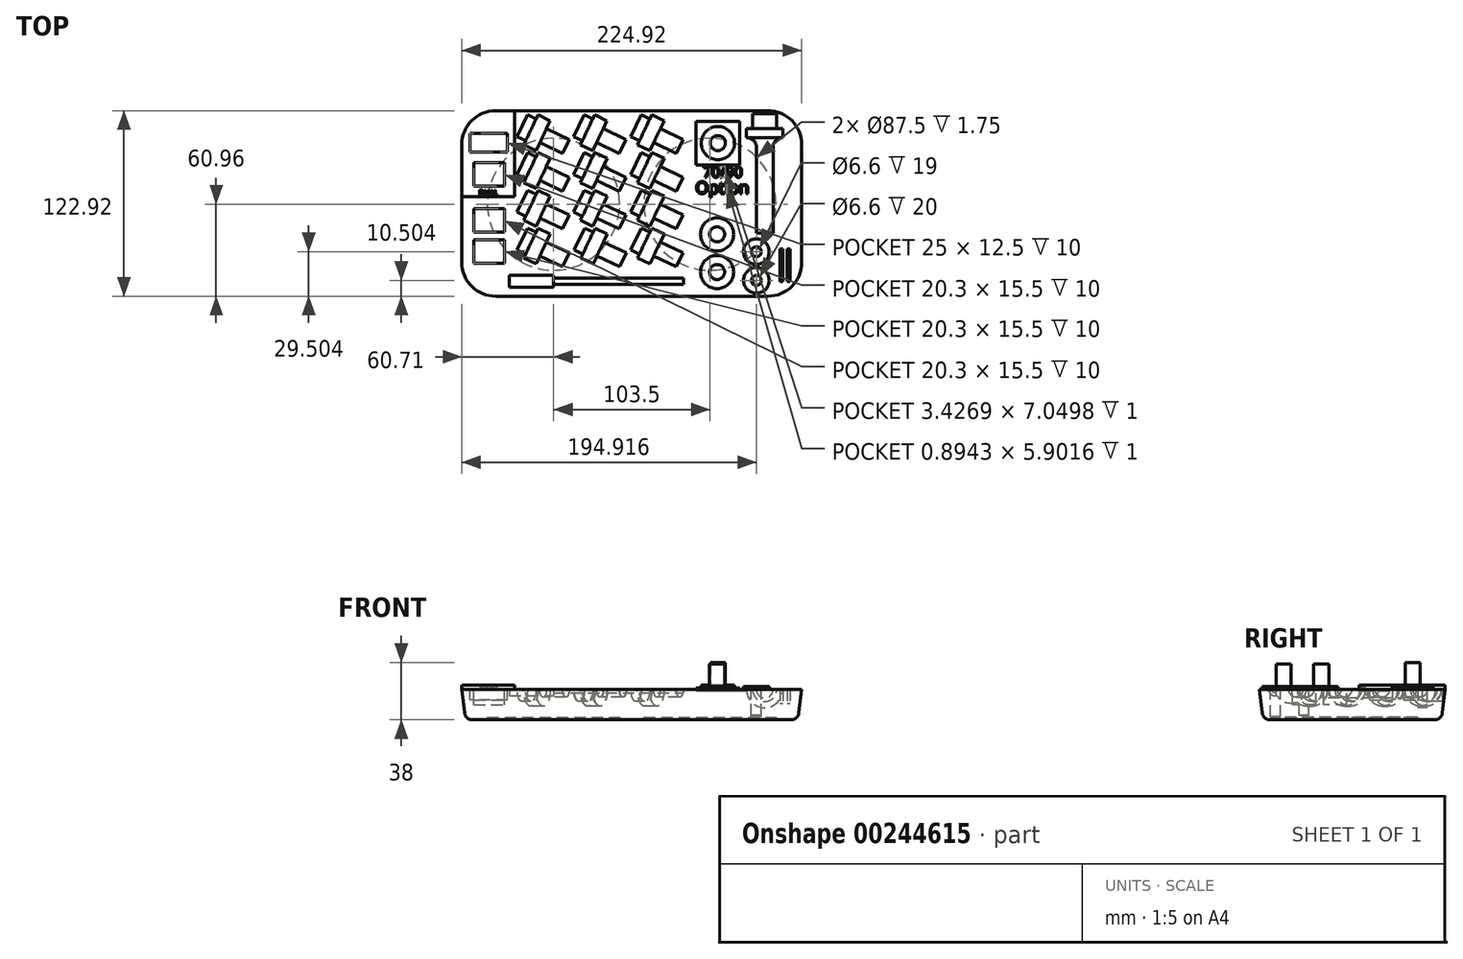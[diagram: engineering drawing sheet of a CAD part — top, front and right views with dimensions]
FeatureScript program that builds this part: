
annotation { "Feature Type Name" : "Feature", "Feature Type Description" : "" }
export const myFeature = defineFeature(function(context is Context, id is Id, definition is map)
    precondition{}
    {
        {
            var Q0;
            Q0=qCreatedBy(makeId("Top.planeOp"),FACE);
            var sketch = newSketch(context, id + "F0", { "sketchPlane" : qUnion([Q0])});
            skLineSegment(sketch, "E0.bottom", {"start": v(20, 0) * mm, "end": v(200, 0) * mm});
            skLineSegment(sketch, "E0.top", {"start": v(20, 118) * mm, "end": v(200, 118) * mm});
            skLineSegment(sketch, "E0.left", {"start": v(0, 20) * mm, "end": v(0, 98) * mm});
            skLineSegment(sketch, "E0.right", {"start": v(220, 20) * mm, "end": v(220, 98) * mm});
            skPoint(sketch, "E1.visualSharp", {"position": v(0, 118) * mm});
            skArc(sketch, "E1.filletArc", {"start": v(20, 118) * mm, "mid": v(5.86, 112.14) * mm, "end": v(0, 98) * mm});
            skPoint(sketch, "E2.visualSharp", {"position": v(220, 118) * mm});
            skArc(sketch, "E2.filletArc", {"start": v(220, 98) * mm, "mid": v(214.14, 112.14) * mm, "end": v(200, 118) * mm});
            skPoint(sketch, "E3.visualSharp", {"position": v(0, 0) * mm});
            skArc(sketch, "E3.filletArc", {"start": v(0, 20) * mm, "mid": v(5.86, 5.86) * mm, "end": v(20, 0) * mm});
            skPoint(sketch, "E4.visualSharp", {"position": v(220, 0) * mm});
            skArc(sketch, "E4.filletArc", {"start": v(200, 0) * mm, "mid": v(214.14, 5.86) * mm, "end": v(220, 20) * mm});
            skSolve(sketch);
        }
        {
            var Q0;
            Q0=makeQuery(id+"F0.imprint","IMPRINT",FACE,{"disambiguationData":[TD([[makeQuery(id+"F0.imprint","IMPRINT",EDGE,{"derivedFrom":sQuery(id+"F0.wireOp",EDGE,"E0.bottom")}),1.0]])]});
            extrude(context, id + "F1", {"entities" : qUnion([Q0]), "depth" : 20 * mm, "hasDraft" : true, "draftAngle" : 7 * degree});
        }
        {
            var Q0;
            Q0=makeQuery(id+"F1.opExtrude","CAP_FACE",FACE,{"disambiguationData":[OSD([sQuery(id+"F0.wireOp",EDGE,"E0.bottom"),sQuery(id+"F0.wireOp",EDGE,"E0.top"),sQuery(id+"F0.wireOp",EDGE,"E0.left"),sQuery(id+"F0.wireOp",EDGE,"E0.right"),sQuery(id+"F0.wireOp",EDGE,"E1.filletArc"),sQuery(id+"F0.wireOp",EDGE,"E2.filletArc"),sQuery(id+"F0.wireOp",EDGE,"E3.filletArc"),sQuery(id+"F0.wireOp",EDGE,"E4.filletArc")])],"isStart":true});
            fillet(context, id + "F2", {"entities" : qUnion([Q0]), "radius" : 5 * mm, "tangentPropagation" : true, "allowEdgeOverflow" : false});
        }
        {
            var Q0;
            Q0=makeQuery(id+"F1.opExtrude","CAP_FACE",FACE,{"disambiguationData":[OSD([sQuery(id+"F0.wireOp",EDGE,"E0.bottom"),sQuery(id+"F0.wireOp",EDGE,"E0.top"),sQuery(id+"F0.wireOp",EDGE,"E0.left"),sQuery(id+"F0.wireOp",EDGE,"E0.right"),sQuery(id+"F0.wireOp",EDGE,"E1.filletArc"),sQuery(id+"F0.wireOp",EDGE,"E2.filletArc"),sQuery(id+"F0.wireOp",EDGE,"E3.filletArc"),sQuery(id+"F0.wireOp",EDGE,"E4.filletArc")])],"isStart":true});
            var sketch = newSketch(context, id + "F3", { "sketchPlane" : qUnion([Q0])});
            skLineSegment(sketch, "E5.bottom", {"start": v(0, 0) * mm, "end": v(58.25, 0) * mm, "construction": true});
            skLineSegment(sketch, "E5.top", {"start": v(0, -58.5) * mm, "end": v(58.25, -58.5) * mm, "construction": true});
            skLineSegment(sketch, "E5.left", {"start": v(0, 0) * mm, "end": v(0, -58.5) * mm, "construction": true});
            skLineSegment(sketch, "E5.right", {"start": v(58.25, 0) * mm, "end": v(58.25, -58.5) * mm, "construction": true});
            skLineSegment(sketch, "E6.bottom", {"start": v(0, 0) * mm, "end": v(161.75, 0) * mm, "construction": true});
            skLineSegment(sketch, "E6.top", {"start": v(0, -58.5) * mm, "end": v(161.75, -58.5) * mm, "construction": true});
            skLineSegment(sketch, "E6.right", {"start": v(161.75, 0) * mm, "end": v(161.75, -58.5) * mm, "construction": true});
            skCircle(sketch, "E7", {"center": v(58.25, -58.5) * mm, "radius": 43.75 * mm});
            skCircle(sketch, "E8", {"center": v(161.75, -58.5) * mm, "radius": 43.75 * mm});
            skSolve(sketch);
        }
        {
            var Q0;
            Q0=qSketchRegion(id+"F3",true);
            extrude(context, id + "F4", {"entities" : qUnion([Q0]), "operationType" : NewBodyOperationType.REMOVE, "oppositeDirection" : true, "depth" : 1.75 * mm});
        }
        {
            var Q0;
            Q0=makeQuery(id+"F1.opExtrude","CAP_FACE",FACE,{"disambiguationData":[OSD([sQuery(id+"F0.wireOp",EDGE,"E0.bottom"),sQuery(id+"F0.wireOp",EDGE,"E0.top"),sQuery(id+"F0.wireOp",EDGE,"E0.left"),sQuery(id+"F0.wireOp",EDGE,"E0.right"),sQuery(id+"F0.wireOp",EDGE,"E1.filletArc"),sQuery(id+"F0.wireOp",EDGE,"E2.filletArc"),sQuery(id+"F0.wireOp",EDGE,"E3.filletArc"),sQuery(id+"F0.wireOp",EDGE,"E4.filletArc")])],"isStart":false});
            var sketch = newSketch(context, id + "F5", { "sketchPlane" : qUnion([Q0])});
            skLineSegment(sketch, "E9.bottom", {"start": v(-2.46, 63.45) * mm, "end": v(32.54, 63.45) * mm});
            skLineSegment(sketch, "E9.top", {"start": v(-2.46, 120.46) * mm, "end": v(32.54, 120.46) * mm});
            skLineSegment(sketch, "E9.left", {"start": v(-2.46, 63.45) * mm, "end": v(-2.46, 120.46) * mm});
            skLineSegment(sketch, "E9.right", {"start": v(32.54, 63.45) * mm, "end": v(32.54, 120.46) * mm});
            skSolve(sketch);
        }
        {
            var Q0;
            {var subQ1=sQuery(id+"F5.wireOp",EDGE,"E9.bottom");Q0=makeQuery(id+"F5.imprint","IMPRINT",FACE,{"disambiguationData":[TD([[makeQuery(id+"F5.imprint","IMPRINT",EDGE,{"derivedFrom":subQ1}),1.0]])]});}
            extrude(context, id + "F6", {"entities" : qUnion([Q0]), "operationType" : NewBodyOperationType.ADD, "depth" : 3 * mm});
        }
        {
            var Q0;
            Q0=makeQuery(id+"F6.opExtrude","CAP_FACE",FACE,{"disambiguationData":[OSD([sQuery(id+"F0.wireOp",EDGE,"E1.filletArc"),sQuery(id+"F5.wireOp",EDGE,"E9.bottom"),sQuery(id+"F5.wireOp",EDGE,"E9.top"),sQuery(id+"F5.wireOp",EDGE,"E9.left"),sQuery(id+"F5.wireOp",EDGE,"E9.right")])],"isStart":false});
            var sketch = newSketch(context, id + "F7", { "sketchPlane" : qUnion([Q0])});
            skText(sketch, "E10", { "text": "DUAL\n", "fontName": "OpenSans-Regular.ttf"});
            const initialGuessF7  = {"E10": [0.00892, 0.06446, 1, 0, 0.00342]};
            skSetInitialGuess(sketch, initialGuessF7);
            skSolve(sketch);
        }
        {
            var Q0;
            Q0=qSketchRegion(id+"F7",true);
            extrude(context, id + "F8", {"entities" : qUnion([Q0]), "operationType" : NewBodyOperationType.REMOVE, "oppositeDirection" : true, "depth" : 1 * mm});
        }
        {
            var Q0;
            {var subQ0=sQuery(id+"F5.wireOp",EDGE,"E9.left");var subQ1=sQuery(id+"F5.wireOp",EDGE,"E9.top");var subQ2=sQuery(id+"F5.wireOp",EDGE,"E9.bottom");var subQ3=sQuery(id+"F5.wireOp",EDGE,"E9.right");var subQ4=sQuery(id+"F0.wireOp",EDGE,"E1.filletArc");Q0=makeQuery(id+"F8.boolean.opBoolean","SPLIT",FACE,{"disambiguationData":[TD([makeQuery(id+"F6.opExtrude","SWEPT_FACE",FACE,{"disambiguationData":[OSD([subQ2])]})])],"derivedFrom":makeQuery(id+"F6.opExtrude","CAP_FACE",FACE,{"disambiguationData":[OSD([subQ4,subQ2,subQ1,subQ0,subQ3])],"isStart":false})});}
            var sketch = newSketch(context, id + "F9", { "sketchPlane" : qUnion([Q0])});
            skSolve(sketch);
        }
        {
            var Q0;
            Q0=makeQuery(id+"F9.imprint","IMPRINT",FACE,{"disambiguationData":[TD([[makeQuery(id+"F9.imprint","IMPRINT",EDGE,{"derivedFrom":makeQuery(id+"F6.opExtrude","CAP_EDGE",EDGE,{"disambiguationData":[OSD([sQuery(id+"F5.wireOp",EDGE,"E9.bottom")])],"isStart":false})}),1.0]])]});
            var sketch = newSketch(context, id + "F10", { "sketchPlane" : qUnion([Q0])});
            skLineSegment(sketch, "E11.bottom", {"start": v(5.54, 70.45) * mm, "end": v(25.84, 70.45) * mm});
            skLineSegment(sketch, "E11.top", {"start": v(5.54, 85.95) * mm, "end": v(25.84, 85.95) * mm});
            skLineSegment(sketch, "E11.left", {"start": v(5.54, 70.45) * mm, "end": v(5.54, 85.95) * mm});
            skLineSegment(sketch, "E11.right", {"start": v(25.84, 70.45) * mm, "end": v(25.84, 85.95) * mm});
            skLineSegment(sketch, "E12.bottom", {"start": v(27.82, 92.95) * mm, "end": v(2.82, 92.95) * mm});
            skLineSegment(sketch, "E12.top", {"start": v(27.82, 105.45) * mm, "end": v(2.82, 105.45) * mm});
            skLineSegment(sketch, "E12.left", {"start": v(27.82, 92.95) * mm, "end": v(27.82, 105.45) * mm});
            skLineSegment(sketch, "E12.right", {"start": v(2.82, 92.95) * mm, "end": v(2.82, 105.45) * mm});
            skSolve(sketch);
        }
        {
            var Q0;
            Q0=qSketchRegion(id+"F10",true);
            extrude(context, id + "F11", {"entities" : qUnion([Q0]), "operationType" : NewBodyOperationType.REMOVE, "oppositeDirection" : true, "depth" : 10 * mm});
        }
        {
            var Q0;
            Q0=makeQuery(id+"F1.opExtrude","CAP_FACE",FACE,{"disambiguationData":[OSD([sQuery(id+"F0.wireOp",EDGE,"E0.bottom"),sQuery(id+"F0.wireOp",EDGE,"E0.top"),sQuery(id+"F0.wireOp",EDGE,"E0.left"),sQuery(id+"F0.wireOp",EDGE,"E0.right"),sQuery(id+"F0.wireOp",EDGE,"E1.filletArc"),sQuery(id+"F0.wireOp",EDGE,"E2.filletArc"),sQuery(id+"F0.wireOp",EDGE,"E3.filletArc"),sQuery(id+"F0.wireOp",EDGE,"E4.filletArc")])],"isStart":false});
            var sketch = newSketch(context, id + "F12", { "sketchPlane" : qUnion([Q0])});
            skLineSegment(sketch, "E13.bottom", {"start": v(5.54, 55.45) * mm, "end": v(25.84, 55.45) * mm});
            skLineSegment(sketch, "E13.top", {"start": v(5.54, 39.95) * mm, "end": v(25.84, 39.95) * mm});
            skLineSegment(sketch, "E13.left", {"start": v(5.54, 55.45) * mm, "end": v(5.54, 39.95) * mm});
            skLineSegment(sketch, "E13.right", {"start": v(25.84, 55.45) * mm, "end": v(25.84, 39.95) * mm});
            skLineSegment(sketch, "E14.bottom", {"start": v(5.54, 34.95) * mm, "end": v(25.84, 34.95) * mm});
            skLineSegment(sketch, "E14.top", {"start": v(5.54, 19.45) * mm, "end": v(25.84, 19.45) * mm});
            skLineSegment(sketch, "E14.left", {"start": v(5.54, 34.95) * mm, "end": v(5.54, 19.45) * mm});
            skLineSegment(sketch, "E14.right", {"start": v(25.84, 34.95) * mm, "end": v(25.84, 19.45) * mm});
            skSolve(sketch);
        }
        {
            var Q0;
            Q0=qSketchRegion(id+"F12",true);
            extrude(context, id + "F13", {"entities" : qUnion([Q0]), "operationType" : NewBodyOperationType.REMOVE, "oppositeDirection" : true, "depth" : 10 * mm});
        }
        {
            var Q0;
            Q0=makeQuery(id+"F1.opExtrude","CAP_FACE",FACE,{"disambiguationData":[OSD([sQuery(id+"F0.wireOp",EDGE,"E0.bottom"),sQuery(id+"F0.wireOp",EDGE,"E0.top"),sQuery(id+"F0.wireOp",EDGE,"E0.left"),sQuery(id+"F0.wireOp",EDGE,"E0.right"),sQuery(id+"F0.wireOp",EDGE,"E1.filletArc"),sQuery(id+"F0.wireOp",EDGE,"E2.filletArc"),sQuery(id+"F0.wireOp",EDGE,"E3.filletArc"),sQuery(id+"F0.wireOp",EDGE,"E4.filletArc")])],"isStart":false});
            var sketch = newSketch(context, id + "F14", { "sketchPlane" : qUnion([Q0])});
            skLineSegment(sketch, "E15", {"start": v(37.54, 110.46) * mm, "end": v(67.13, 96.37) * mm, "construction": true});
            skLineSegment(sketch, "E16", {"start": v(37.54, 110.46) * mm, "end": v(40.98, 117.68) * mm});
            skLineSegment(sketch, "E17", {"start": v(40.98, 117.68) * mm, "end": v(46.67, 114.97) * mm});
            skLineSegment(sketch, "E18", {"start": v(46.67, 114.97) * mm, "end": v(47.96, 117.68) * mm});
            skLineSegment(sketch, "E19", {"start": v(47.96, 117.68) * mm, "end": v(56.09, 113.8) * mm});
            skLineSegment(sketch, "E20", {"start": v(56.09, 113.8) * mm, "end": v(53.55, 108.48) * mm});
            skLineSegment(sketch, "E21", {"start": v(53.55, 108.48) * mm, "end": v(68.63, 101.3) * mm});
            skLineSegment(sketch, "E22", {"start": v(68.63, 101.3) * mm, "end": v(66.44, 96.7) * mm});
            skLineSegment(sketch, "E23", {"start": v(66.44, 96.7) * mm, "end": v(37.54, 110.46) * mm});
            skLineSegment(sketch, "E24.bottom", {"start": v(37.54, 110.46) * mm, "end": v(75.04, 110.46) * mm, "construction": true});
            skLineSegment(sketch, "E24.top", {"start": v(37.54, 85.46) * mm, "end": v(75.04, 85.46) * mm, "construction": true});
            skLineSegment(sketch, "E24.left", {"start": v(37.54, 110.46) * mm, "end": v(37.54, 85.46) * mm, "construction": true});
            skLineSegment(sketch, "E24.right", {"start": v(75.04, 110.46) * mm, "end": v(75.04, 85.46) * mm, "construction": true});
            skLineSegment(sketch, "E25", {"start": v(37.54, 85.46) * mm, "end": v(40.98, 92.68) * mm});
            skLineSegment(sketch, "E26", {"start": v(40.98, 92.68) * mm, "end": v(46.67, 89.97) * mm});
            skLineSegment(sketch, "E27", {"start": v(46.67, 89.97) * mm, "end": v(47.96, 92.68) * mm});
            skLineSegment(sketch, "E28", {"start": v(47.96, 92.68) * mm, "end": v(56.09, 88.8) * mm});
            skLineSegment(sketch, "E29", {"start": v(56.09, 88.8) * mm, "end": v(53.55, 83.48) * mm});
            skLineSegment(sketch, "E30", {"start": v(53.55, 83.48) * mm, "end": v(68.63, 76.3) * mm});
            skLineSegment(sketch, "E31", {"start": v(68.63, 76.3) * mm, "end": v(66.44, 71.7) * mm});
            skLineSegment(sketch, "E32", {"start": v(66.44, 71.7) * mm, "end": v(37.54, 85.46) * mm});
            skLineSegment(sketch, "E33.bottom", {"start": v(37.54, 85.46) * mm, "end": v(75.06, 85.46) * mm, "construction": true});
            skLineSegment(sketch, "E33.top", {"start": v(37.54, 60.46) * mm, "end": v(75.06, 60.46) * mm, "construction": true});
            skLineSegment(sketch, "E33.left", {"start": v(37.54, 85.46) * mm, "end": v(37.54, 60.46) * mm, "construction": true});
            skLineSegment(sketch, "E33.right", {"start": v(75.06, 85.46) * mm, "end": v(75.06, 60.46) * mm, "construction": true});
            skLineSegment(sketch, "E34.bottom", {"start": v(37.54, 60.46) * mm, "end": v(75.04, 60.46) * mm, "construction": true});
            skLineSegment(sketch, "E34.top", {"start": v(37.54, 35.46) * mm, "end": v(75.04, 35.46) * mm, "construction": true});
            skLineSegment(sketch, "E34.left", {"start": v(37.54, 60.46) * mm, "end": v(37.54, 35.46) * mm, "construction": true});
            skLineSegment(sketch, "E34.right", {"start": v(75.04, 60.46) * mm, "end": v(75.04, 35.46) * mm, "construction": true});
            skLineSegment(sketch, "E35.bottom", {"start": v(37.54, 35.46) * mm, "end": v(75.34, 35.46) * mm, "construction": true});
            skLineSegment(sketch, "E35.top", {"start": v(37.54, 10.46) * mm, "end": v(75.34, 10.46) * mm, "construction": true});
            skLineSegment(sketch, "E35.left", {"start": v(37.54, 35.46) * mm, "end": v(37.54, 10.46) * mm, "construction": true});
            skLineSegment(sketch, "E35.right", {"start": v(75.34, 35.46) * mm, "end": v(75.34, 10.46) * mm, "construction": true});
            skLineSegment(sketch, "E36.bottom", {"start": v(75.04, 110.46) * mm, "end": v(112.84, 110.46) * mm, "construction": true});
            skLineSegment(sketch, "E36.top", {"start": v(75.04, 85.46) * mm, "end": v(112.84, 85.46) * mm, "construction": true});
            skLineSegment(sketch, "E36.right", {"start": v(112.84, 110.46) * mm, "end": v(112.84, 85.46) * mm, "construction": true});
            skLineSegment(sketch, "E37.bottom", {"start": v(75.06, 85.46) * mm, "end": v(112.84, 85.46) * mm, "construction": true});
            skLineSegment(sketch, "E37.top", {"start": v(75.06, 60.46) * mm, "end": v(112.84, 60.46) * mm, "construction": true});
            skLineSegment(sketch, "E37.right", {"start": v(112.84, 85.46) * mm, "end": v(112.84, 60.46) * mm, "construction": true});
            skLineSegment(sketch, "E38.top", {"start": v(75.06, 35.46) * mm, "end": v(112.84, 35.46) * mm, "construction": true});
            skLineSegment(sketch, "E38.left", {"start": v(75.06, 60.46) * mm, "end": v(75.06, 35.46) * mm, "construction": true});
            skLineSegment(sketch, "E38.right", {"start": v(112.84, 60.46) * mm, "end": v(112.84, 35.46) * mm, "construction": true});
            skLineSegment(sketch, "E39.bottom", {"start": v(75.34, 35.46) * mm, "end": v(112.84, 35.46) * mm, "construction": true});
            skLineSegment(sketch, "E39.top", {"start": v(75.34, 10.46) * mm, "end": v(112.84, 10.46) * mm, "construction": true});
            skLineSegment(sketch, "E39.right", {"start": v(112.84, 35.46) * mm, "end": v(112.84, 10.46) * mm, "construction": true});
            skLineSegment(sketch, "E40.bottom", {"start": v(112.84, 110.46) * mm, "end": v(150.64, 110.46) * mm, "construction": true});
            skLineSegment(sketch, "E40.top", {"start": v(112.84, 85.46) * mm, "end": v(150.64, 85.46) * mm, "construction": true});
            skLineSegment(sketch, "E40.right", {"start": v(150.64, 110.46) * mm, "end": v(150.64, 85.46) * mm, "construction": true});
            skLineSegment(sketch, "E41.top", {"start": v(112.84, 60.46) * mm, "end": v(150.64, 60.46) * mm, "construction": true});
            skLineSegment(sketch, "E41.right", {"start": v(150.64, 85.46) * mm, "end": v(150.64, 60.46) * mm, "construction": true});
            skLineSegment(sketch, "E42.top", {"start": v(112.84, 35.46) * mm, "end": v(150.64, 35.46) * mm, "construction": true});
            skLineSegment(sketch, "E42.right", {"start": v(150.64, 60.46) * mm, "end": v(150.64, 35.46) * mm, "construction": true});
            skLineSegment(sketch, "E43.top", {"start": v(112.84, 10.46) * mm, "end": v(150.64, 10.46) * mm, "construction": true});
            skLineSegment(sketch, "E43.right", {"start": v(150.64, 35.46) * mm, "end": v(150.64, 10.46) * mm, "construction": true});
            skLineSegment(sketch, "E44", {"start": v(37.54, 60.46) * mm, "end": v(40.98, 67.68) * mm});
            skLineSegment(sketch, "E45", {"start": v(37.54, 35.46) * mm, "end": v(40.98, 42.68) * mm});
            skLineSegment(sketch, "E46", {"start": v(75.04, 110.46) * mm, "end": v(78.48, 117.68) * mm});
            skLineSegment(sketch, "E47", {"start": v(75.06, 85.46) * mm, "end": v(78.5, 92.68) * mm});
            skLineSegment(sketch, "E48", {"start": v(75.06, 60.46) * mm, "end": v(78.5, 67.68) * mm});
            skPoint(sketch, "E49.endSnap0", {"position": v(75.06, 47.96) * mm});
            skLineSegment(sketch, "E50", {"start": v(75.34, 35.46) * mm, "end": v(78.78, 42.68) * mm});
            skLineSegment(sketch, "E51", {"start": v(112.84, 35.46) * mm, "end": v(116.28, 42.68) * mm});
            skLineSegment(sketch, "E52", {"start": v(112.84, 60.46) * mm, "end": v(116.28, 67.68) * mm});
            skLineSegment(sketch, "E53", {"start": v(112.84, 85.46) * mm, "end": v(116.28, 92.68) * mm});
            skLineSegment(sketch, "E54", {"start": v(112.84, 110.46) * mm, "end": v(116.28, 117.68) * mm});
            skLineSegment(sketch, "E55", {"start": v(40.98, 67.68) * mm, "end": v(46.67, 64.97) * mm});
            skLineSegment(sketch, "E56", {"start": v(46.67, 64.97) * mm, "end": v(47.96, 67.68) * mm});
            skLineSegment(sketch, "E57", {"start": v(47.96, 67.68) * mm, "end": v(56.09, 63.8) * mm});
            skLineSegment(sketch, "E58", {"start": v(56.09, 63.8) * mm, "end": v(53.55, 58.48) * mm});
            skLineSegment(sketch, "E59", {"start": v(40.98, 42.68) * mm, "end": v(46.67, 39.97) * mm});
            skLineSegment(sketch, "E60", {"start": v(46.67, 39.97) * mm, "end": v(47.96, 42.68) * mm});
            skLineSegment(sketch, "E61", {"start": v(47.96, 42.68) * mm, "end": v(56.09, 38.8) * mm});
            skLineSegment(sketch, "E62", {"start": v(56.09, 38.8) * mm, "end": v(53.55, 33.48) * mm});
            skLineSegment(sketch, "E63", {"start": v(53.55, 33.48) * mm, "end": v(68.63, 26.3) * mm});
            skLineSegment(sketch, "E64", {"start": v(68.63, 26.3) * mm, "end": v(66.44, 21.7) * mm});
            skLineSegment(sketch, "E65", {"start": v(66.44, 21.7) * mm, "end": v(37.54, 35.46) * mm});
            skLineSegment(sketch, "E66", {"start": v(53.55, 58.48) * mm, "end": v(68.63, 51.3) * mm});
            skLineSegment(sketch, "E67", {"start": v(68.63, 51.3) * mm, "end": v(66.44, 46.7) * mm});
            skLineSegment(sketch, "E68", {"start": v(66.44, 46.7) * mm, "end": v(37.54, 60.46) * mm});
            skLineSegment(sketch, "E69", {"start": v(78.48, 117.68) * mm, "end": v(84.17, 114.97) * mm});
            skLineSegment(sketch, "E70", {"start": v(84.17, 114.97) * mm, "end": v(85.46, 117.68) * mm});
            skLineSegment(sketch, "E71", {"start": v(85.46, 117.68) * mm, "end": v(93.59, 113.8) * mm});
            skLineSegment(sketch, "E72", {"start": v(93.59, 113.8) * mm, "end": v(91.05, 108.48) * mm});
            skLineSegment(sketch, "E73", {"start": v(91.05, 108.48) * mm, "end": v(106.13, 101.3) * mm});
            skLineSegment(sketch, "E74", {"start": v(106.13, 101.3) * mm, "end": v(103.94, 96.7) * mm});
            skLineSegment(sketch, "E75", {"start": v(103.94, 96.7) * mm, "end": v(75.04, 110.46) * mm});
            skLineSegment(sketch, "E76", {"start": v(78.5, 92.68) * mm, "end": v(84.19, 89.97) * mm});
            skLineSegment(sketch, "E77", {"start": v(84.19, 89.97) * mm, "end": v(85.48, 92.68) * mm});
            skLineSegment(sketch, "E78", {"start": v(85.48, 92.68) * mm, "end": v(93.6, 88.8) * mm});
            skLineSegment(sketch, "E79", {"start": v(93.6, 88.8) * mm, "end": v(91.07, 83.48) * mm});
            skLineSegment(sketch, "E80", {"start": v(91.07, 83.48) * mm, "end": v(106.14, 76.3) * mm});
            skLineSegment(sketch, "E81", {"start": v(106.14, 76.3) * mm, "end": v(103.95, 71.7) * mm});
            skLineSegment(sketch, "E82", {"start": v(103.95, 71.7) * mm, "end": v(75.06, 85.46) * mm});
            skLineSegment(sketch, "E83", {"start": v(78.5, 67.68) * mm, "end": v(84.19, 64.97) * mm});
            skLineSegment(sketch, "E84", {"start": v(84.19, 64.97) * mm, "end": v(85.48, 67.68) * mm});
            skLineSegment(sketch, "E85", {"start": v(85.48, 67.68) * mm, "end": v(93.6, 63.8) * mm});
            skLineSegment(sketch, "E86", {"start": v(93.6, 63.8) * mm, "end": v(91.07, 58.48) * mm});
            skLineSegment(sketch, "E87", {"start": v(91.07, 58.48) * mm, "end": v(106.14, 51.3) * mm});
            skLineSegment(sketch, "E88", {"start": v(106.14, 51.3) * mm, "end": v(103.95, 46.7) * mm});
            skLineSegment(sketch, "E89", {"start": v(103.95, 46.7) * mm, "end": v(75.06, 60.46) * mm});
            skLineSegment(sketch, "E90", {"start": v(78.78, 42.68) * mm, "end": v(84.47, 39.97) * mm});
            skLineSegment(sketch, "E91", {"start": v(84.47, 39.97) * mm, "end": v(85.76, 42.68) * mm});
            skLineSegment(sketch, "E92", {"start": v(85.76, 42.68) * mm, "end": v(93.88, 38.8) * mm});
            skLineSegment(sketch, "E93", {"start": v(93.88, 38.8) * mm, "end": v(91.35, 33.48) * mm});
            skLineSegment(sketch, "E94", {"start": v(91.35, 33.48) * mm, "end": v(106.42, 26.3) * mm});
            skLineSegment(sketch, "E95", {"start": v(106.42, 26.3) * mm, "end": v(104.23, 21.7) * mm});
            skLineSegment(sketch, "E96", {"start": v(104.23, 21.7) * mm, "end": v(75.34, 35.46) * mm});
            skLineSegment(sketch, "E97", {"start": v(116.28, 117.68) * mm, "end": v(121.97, 114.97) * mm});
            skLineSegment(sketch, "E98", {"start": v(121.97, 114.97) * mm, "end": v(123.26, 117.68) * mm});
            skLineSegment(sketch, "E99", {"start": v(123.26, 117.68) * mm, "end": v(131.38, 113.8) * mm});
            skLineSegment(sketch, "E100", {"start": v(131.38, 113.8) * mm, "end": v(128.85, 108.48) * mm});
            skLineSegment(sketch, "E101", {"start": v(128.85, 108.48) * mm, "end": v(143.92, 101.3) * mm});
            skLineSegment(sketch, "E102", {"start": v(143.92, 101.3) * mm, "end": v(141.73, 96.7) * mm});
            skLineSegment(sketch, "E103", {"start": v(141.73, 96.7) * mm, "end": v(112.84, 110.46) * mm});
            skLineSegment(sketch, "E104", {"start": v(116.28, 92.68) * mm, "end": v(121.97, 89.97) * mm});
            skLineSegment(sketch, "E105", {"start": v(121.97, 89.97) * mm, "end": v(123.26, 92.68) * mm});
            skLineSegment(sketch, "E106", {"start": v(123.26, 92.68) * mm, "end": v(131.38, 88.8) * mm});
            skLineSegment(sketch, "E107", {"start": v(131.38, 88.8) * mm, "end": v(128.85, 83.48) * mm});
            skLineSegment(sketch, "E108", {"start": v(128.85, 83.48) * mm, "end": v(143.92, 76.3) * mm});
            skLineSegment(sketch, "E109", {"start": v(143.92, 76.3) * mm, "end": v(141.73, 71.7) * mm});
            skLineSegment(sketch, "E110", {"start": v(141.73, 71.7) * mm, "end": v(112.84, 85.46) * mm});
            skLineSegment(sketch, "E111", {"start": v(116.28, 67.68) * mm, "end": v(121.97, 64.97) * mm});
            skLineSegment(sketch, "E112", {"start": v(121.97, 64.97) * mm, "end": v(123.26, 67.68) * mm});
            skLineSegment(sketch, "E113", {"start": v(123.26, 67.68) * mm, "end": v(131.38, 63.8) * mm});
            skLineSegment(sketch, "E114", {"start": v(131.38, 63.8) * mm, "end": v(128.85, 58.48) * mm});
            skLineSegment(sketch, "E115", {"start": v(128.85, 58.48) * mm, "end": v(143.92, 51.3) * mm});
            skLineSegment(sketch, "E116", {"start": v(143.92, 51.3) * mm, "end": v(141.73, 46.7) * mm});
            skLineSegment(sketch, "E117", {"start": v(141.73, 46.7) * mm, "end": v(112.84, 60.46) * mm});
            skLineSegment(sketch, "E118", {"start": v(116.28, 42.68) * mm, "end": v(121.97, 39.97) * mm});
            skLineSegment(sketch, "E119", {"start": v(121.97, 39.97) * mm, "end": v(123.26, 42.68) * mm});
            skLineSegment(sketch, "E120", {"start": v(123.26, 42.68) * mm, "end": v(131.38, 38.8) * mm});
            skLineSegment(sketch, "E121", {"start": v(131.38, 38.8) * mm, "end": v(128.85, 33.48) * mm});
            skLineSegment(sketch, "E122", {"start": v(128.85, 33.48) * mm, "end": v(143.92, 26.3) * mm});
            skLineSegment(sketch, "E123", {"start": v(143.92, 26.3) * mm, "end": v(141.73, 21.7) * mm});
            skLineSegment(sketch, "E124", {"start": v(141.73, 21.7) * mm, "end": v(112.84, 35.46) * mm});
            skSolve(sketch);
        }
        {
            var Q0;
            Q0=makeQuery(id+"F14.imprint","IMPRINT",FACE,{"disambiguationData":[TD([[makeQuery(id+"F14.imprint","IMPRINT",EDGE,{"derivedFrom":sQuery(id+"F14.wireOp",EDGE,"E16")}),-1.0]])]});
            var Q1;
            Q1=sQuery(id+"F14.wireOp",EDGE,"E23");
            revolve(context, id + "F15", {"operationType" : NewBodyOperationType.REMOVE, "entities" : qUnion([Q0]), "axis" : qUnion([Q1]), "revolveType" : RevolveType.FULL, "oppositeDirection" : true});
        }
        {
            var Q0;
            Q0=makeQuery(id+"F14.imprint","IMPRINT",FACE,{"disambiguationData":[TD([[makeQuery(id+"F14.imprint","IMPRINT",EDGE,{"derivedFrom":sQuery(id+"F14.wireOp",EDGE,"E25")}),-1.0]])]});
            var Q1;
            Q1=sQuery(id+"F14.wireOp",EDGE,"E32");
            revolve(context, id + "F16", {"operationType" : NewBodyOperationType.REMOVE, "entities" : qUnion([Q0]), "axis" : qUnion([Q1]), "revolveType" : RevolveType.FULL, "oppositeDirection" : true});
        }
        {
            var Q0;
            Q0=makeQuery(id+"F14.imprint","IMPRINT",FACE,{"disambiguationData":[TD([[makeQuery(id+"F14.imprint","IMPRINT",EDGE,{"derivedFrom":sQuery(id+"F14.wireOp",EDGE,"E44")}),-1.0]])]});
            var Q1;
            Q1=sQuery(id+"F14.wireOp",EDGE,"E68");
            revolve(context, id + "F17", {"operationType" : NewBodyOperationType.REMOVE, "entities" : qUnion([Q0]), "axis" : qUnion([Q1]), "revolveType" : RevolveType.FULL, "oppositeDirection" : true});
        }
        {
            var Q0;
            Q0=makeQuery(id+"F14.imprint","IMPRINT",FACE,{"disambiguationData":[TD([[makeQuery(id+"F14.imprint","IMPRINT",EDGE,{"derivedFrom":sQuery(id+"F14.wireOp",EDGE,"E45")}),-1.0]])]});
            var Q1;
            Q1=sQuery(id+"F14.wireOp",EDGE,"E65");
            revolve(context, id + "F18", {"operationType" : NewBodyOperationType.REMOVE, "entities" : qUnion([Q0]), "axis" : qUnion([Q1]), "revolveType" : RevolveType.FULL, "oppositeDirection" : true});
        }
        {
            var Q0;
            Q0=makeQuery(id+"F14.imprint","IMPRINT",FACE,{"disambiguationData":[TD([[makeQuery(id+"F14.imprint","IMPRINT",EDGE,{"derivedFrom":sQuery(id+"F14.wireOp",EDGE,"E46")}),-1.0]])]});
            var Q1;
            Q1=sQuery(id+"F14.wireOp",EDGE,"E75");
            revolve(context, id + "F19", {"operationType" : NewBodyOperationType.REMOVE, "entities" : qUnion([Q0]), "axis" : qUnion([Q1]), "revolveType" : RevolveType.FULL, "oppositeDirection" : true});
        }
        {
            var Q0;
            Q0=makeQuery(id+"F14.imprint","IMPRINT",FACE,{"disambiguationData":[TD([[makeQuery(id+"F14.imprint","IMPRINT",EDGE,{"derivedFrom":sQuery(id+"F14.wireOp",EDGE,"E47")}),-1.0]])]});
            var Q1;
            Q1=sQuery(id+"F14.wireOp",EDGE,"E82");
            revolve(context, id + "F20", {"operationType" : NewBodyOperationType.REMOVE, "entities" : qUnion([Q0]), "axis" : qUnion([Q1]), "revolveType" : RevolveType.FULL, "oppositeDirection" : true});
        }
        {
            var Q0;
            Q0=makeQuery(id+"F14.imprint","IMPRINT",FACE,{"disambiguationData":[TD([[makeQuery(id+"F14.imprint","IMPRINT",EDGE,{"derivedFrom":sQuery(id+"F14.wireOp",EDGE,"E54")}),-1.0]])]});
            var Q1;
            Q1=sQuery(id+"F14.wireOp",EDGE,"E103");
            revolve(context, id + "F21", {"operationType" : NewBodyOperationType.REMOVE, "entities" : qUnion([Q0]), "axis" : qUnion([Q1]), "revolveType" : RevolveType.FULL, "oppositeDirection" : true});
        }
        {
            var Q0;
            Q0=makeQuery(id+"F14.imprint","IMPRINT",FACE,{"disambiguationData":[TD([[makeQuery(id+"F14.imprint","IMPRINT",EDGE,{"derivedFrom":sQuery(id+"F14.wireOp",EDGE,"E51")}),-1.0]])]});
            var Q1;
            Q1=sQuery(id+"F14.wireOp",EDGE,"E124");
            revolve(context, id + "F22", {"operationType" : NewBodyOperationType.REMOVE, "entities" : qUnion([Q0]), "axis" : qUnion([Q1]), "revolveType" : RevolveType.FULL, "oppositeDirection" : true});
        }
        {
            var Q0;
            Q0=makeQuery(id+"F14.imprint","IMPRINT",FACE,{"disambiguationData":[TD([[makeQuery(id+"F14.imprint","IMPRINT",EDGE,{"derivedFrom":sQuery(id+"F14.wireOp",EDGE,"E53")}),-1.0]])]});
            var Q1;
            Q1=sQuery(id+"F14.wireOp",EDGE,"E110");
            revolve(context, id + "F23", {"operationType" : NewBodyOperationType.REMOVE, "entities" : qUnion([Q0]), "axis" : qUnion([Q1]), "revolveType" : RevolveType.FULL, "oppositeDirection" : true});
        }
        {
            var Q0;
            Q0=makeQuery(id+"F14.imprint","IMPRINT",FACE,{"disambiguationData":[TD([[makeQuery(id+"F14.imprint","IMPRINT",EDGE,{"derivedFrom":sQuery(id+"F14.wireOp",EDGE,"E52")}),-1.0]])]});
            var Q1;
            Q1=sQuery(id+"F14.wireOp",EDGE,"E117");
            revolve(context, id + "F24", {"operationType" : NewBodyOperationType.REMOVE, "entities" : qUnion([Q0]), "axis" : qUnion([Q1]), "revolveType" : RevolveType.FULL, "oppositeDirection" : true});
        }
        {
            var Q0;
            Q0=makeQuery(id+"F14.imprint","IMPRINT",FACE,{"disambiguationData":[TD([[makeQuery(id+"F14.imprint","IMPRINT",EDGE,{"derivedFrom":sQuery(id+"F14.wireOp",EDGE,"E48")}),-1.0]])]});
            var Q1;
            Q1=sQuery(id+"F14.wireOp",EDGE,"E89");
            revolve(context, id + "F25", {"operationType" : NewBodyOperationType.REMOVE, "entities" : qUnion([Q0]), "axis" : qUnion([Q1]), "revolveType" : RevolveType.FULL, "oppositeDirection" : true});
        }
        {
            var Q0;
            Q0=makeQuery(id+"F14.imprint","IMPRINT",FACE,{"disambiguationData":[TD([[makeQuery(id+"F14.imprint","IMPRINT",EDGE,{"derivedFrom":sQuery(id+"F14.wireOp",EDGE,"E50")}),-1.0]])]});
            var Q1;
            Q1=sQuery(id+"F14.wireOp",EDGE,"E96");
            revolve(context, id + "F26", {"operationType" : NewBodyOperationType.REMOVE, "entities" : qUnion([Q0]), "axis" : qUnion([Q1]), "revolveType" : RevolveType.FULL, "oppositeDirection" : true});
        }
        {
            var Q0;
            Q0=makeQuery(id+"F14.imprint","IMPRINT",FACE,{"disambiguationData":[TD([[makeQuery(id+"F14.imprint","IMPRINT",EDGE,{"derivedFrom":sQuery(id+"F14.wireOp",EDGE,"E16")}),1.0]])]});
            var sketch = newSketch(context, id + "F27", { "sketchPlane" : qUnion([Q0])});
            skLineSegment(sketch, "E125.bottom", {"start": v(152.46, 113.46) * mm, "end": v(181.46, 113.46) * mm});
            skLineSegment(sketch, "E125.top", {"start": v(152.46, 84.46) * mm, "end": v(181.46, 84.46) * mm});
            skLineSegment(sketch, "E125.left", {"start": v(152.46, 113.46) * mm, "end": v(152.46, 84.46) * mm});
            skLineSegment(sketch, "E125.right", {"start": v(181.46, 113.46) * mm, "end": v(181.46, 84.46) * mm});
            skLineSegment(sketch, "E126", {"start": v(152.46, 84.46) * mm, "end": v(181.46, 113.46) * mm, "construction": true});
            skLineSegment(sketch, "E127", {"start": v(152.46, 113.46) * mm, "end": v(181.46, 84.46) * mm, "construction": true});
            skSolve(sketch);
        }
        {
            var Q0;
            Q0=qSketchRegion(id+"F27",true);
            extrude(context, id + "F28", {"entities" : qUnion([Q0]), "operationType" : NewBodyOperationType.ADD, "depth" : 1 * mm});
        }
        {
            var Q0;
            Q0=makeQuery(id+"F28.opExtrude","CAP_FACE",FACE,{"disambiguationData":[OSD([sQuery(id+"F27.wireOp",EDGE,"E125.bottom"),sQuery(id+"F27.wireOp",EDGE,"E125.top"),sQuery(id+"F27.wireOp",EDGE,"E125.left"),sQuery(id+"F27.wireOp",EDGE,"E125.right")])],"isStart":false});
            var sketch = newSketch(context, id + "F29", { "sketchPlane" : qUnion([Q0])});
            skLineSegment(sketch, "E128", {"start": v(152.46, 84.46) * mm, "end": v(181.46, 113.46) * mm, "construction": true});
            skLineSegment(sketch, "E129", {"start": v(181.46, 113.46) * mm, "end": v(152.46, 113.46) * mm, "construction": true});
            skLineSegment(sketch, "E130", {"start": v(152.46, 113.46) * mm, "end": v(181.46, 84.46) * mm, "construction": true});
            skCircle(sketch, "E131", {"center": v(166.96, 98.96) * mm, "radius": 11 * mm});
            skSolve(sketch);
        }
        {
            var Q0;
            Q0=qSketchRegion(id+"F29",true);
            extrude(context, id + "F30", {"entities" : qUnion([Q0]), "operationType" : NewBodyOperationType.ADD, "depth" : 2 * mm});
        }
        {
            var Q0;
            Q0=makeQuery(id+"F30.opExtrude","CAP_FACE",FACE,{"disambiguationData":[OSD([sQuery(id+"F29.wireOp",EDGE,"E131")])],"isStart":false});
            var sketch = newSketch(context, id + "F31", { "sketchPlane" : qUnion([Q0])});
            skCircle(sketch, "E132", {"center": v(166.96, 98.96) * mm, "radius": 5 * mm});
            skSolve(sketch);
        }
        {
            var Q0;
            Q0=qSketchRegion(id+"F31",true);
            extrude(context, id + "F32", {"entities" : qUnion([Q0]), "operationType" : NewBodyOperationType.ADD, "depth" : 15 * mm});
        }
        {
            var Q0;
            Q0=makeQuery(id+"F14.imprint","IMPRINT",FACE,{"disambiguationData":[TD([[makeQuery(id+"F14.imprint","IMPRINT",EDGE,{"derivedFrom":sQuery(id+"F14.wireOp",EDGE,"E16")}),1.0]])]});
            var sketch = newSketch(context, id + "F33", { "sketchPlane" : qUnion([Q0])});
            skCircle(sketch, "E133", {"center": v(166.46, 38.54) * mm, "radius": 11 * mm});
            skCircle(sketch, "E134", {"center": v(166.46, 13.54) * mm, "radius": 11 * mm});
            skSolve(sketch);
        }
        {
            var Q0;
            Q0=qSketchRegion(id+"F33",true);
            extrude(context, id + "F34", {"entities" : qUnion([Q0]), "operationType" : NewBodyOperationType.ADD, "depth" : 2 * mm});
        }
        {
            var Q0;
            Q0=makeQuery(id+"F34.opExtrude","CAP_FACE",FACE,{"disambiguationData":[OSD([sQuery(id+"F33.wireOp",EDGE,"E133")])],"isStart":false});
            var sketch = newSketch(context, id + "F35", { "sketchPlane" : qUnion([Q0])});
            skCircle(sketch, "E135", {"center": v(166.46, 38.54) * mm, "radius": 5 * mm});
            skSolve(sketch);
        }
        {
            var Q0;
            Q0=makeQuery(id+"F34.opExtrude","CAP_FACE",FACE,{"disambiguationData":[OSD([sQuery(id+"F33.wireOp",EDGE,"E134")])],"isStart":false});
            var sketch = newSketch(context, id + "F36", { "sketchPlane" : qUnion([Q0])});
            skCircle(sketch, "E136", {"center": v(166.46, 13.54) * mm, "radius": 5 * mm});
            skSolve(sketch);
        }
        {
            var Q0;
            Q0=qSketchRegion(id+"F36",true);
            extrude(context, id + "F37", {"entities" : qUnion([Q0]), "operationType" : NewBodyOperationType.ADD, "depth" : 15 * mm});
        }
        {
            var Q0;
            Q0=qSketchRegion(id+"F35",true);
            extrude(context, id + "F38", {"entities" : qUnion([Q0]), "operationType" : NewBodyOperationType.ADD, "depth" : 15 * mm});
        }
        {
            var Q0;
            Q0=makeQuery(id+"F14.imprint","IMPRINT",FACE,{"disambiguationData":[TD([[makeQuery(id+"F14.imprint","IMPRINT",EDGE,{"derivedFrom":sQuery(id+"F14.wireOp",EDGE,"E16")}),1.0]])]});
            var sketch = newSketch(context, id + "F39", { "sketchPlane" : qUnion([Q0])});
            skText(sketch, "E137", { "text": "70/90", "fontName": "OpenSans-Regular.ttf"});
            const initialGuessF39  = {"E137": [0.1571, 0.07634, 1, 0, 0.00711]};
            skSetInitialGuess(sketch, initialGuessF39);
            skSolve(sketch);
        }
        {
            var Q0;
            Q0=qSketchRegion(id+"F39",true);
            extrude(context, id + "F40", {"entities" : qUnion([Q0]), "operationType" : NewBodyOperationType.REMOVE, "oppositeDirection" : true, "depth" : 1 * mm});
        }
        {
            var Q0;
            Q0=makeQuery(id+"F14.imprint","IMPRINT",FACE,{"disambiguationData":[TD([[makeQuery(id+"F14.imprint","IMPRINT",EDGE,{"derivedFrom":sQuery(id+"F14.wireOp",EDGE,"E16")}),1.0]])]});
            var sketch = newSketch(context, id + "F41", { "sketchPlane" : qUnion([Q0])});
            skText(sketch, "E138", { "text": "Option", "fontName": "OpenSans-Regular.ttf"});
            const initialGuessF41  = {"E138": [0.15217, 0.06552, 1, 0, 0.00794]};
            skSetInitialGuess(sketch, initialGuessF41);
            skSolve(sketch);
        }
        {
            var Q0;
            Q0=qSketchRegion(id+"F41",true);
            extrude(context, id + "F42", {"entities" : qUnion([Q0]), "operationType" : NewBodyOperationType.REMOVE, "oppositeDirection" : true, "depth" : 1 * mm});
        }
        {
            var Q0;
            Q0=makeQuery(id+"F14.imprint","IMPRINT",FACE,{"disambiguationData":[TD([[makeQuery(id+"F14.imprint","IMPRINT",EDGE,{"derivedFrom":sQuery(id+"F14.wireOp",EDGE,"E16")}),1.0]])]});
            var sketch = newSketch(context, id + "F43", { "sketchPlane" : qUnion([Q0])});
            skCircle(sketch, "E139", {"center": v(192.46, 8.04) * mm, "radius": 8.5 * mm});
            skLineSegment(sketch, "E140", {"start": v(192.46, 8.04) * mm, "end": v(192.46, 128.14) * mm, "construction": true});
            skCircle(sketch, "E141", {"center": v(192.46, 27.04) * mm, "radius": 8.5 * mm});
            skLineSegment(sketch, "E142.bottom", {"start": v(208.08, 7.15) * mm, "end": v(210.08, 7.15) * mm});
            skLineSegment(sketch, "E142.top", {"start": v(208.08, 18.15) * mm, "end": v(210.08, 18.15) * mm});
            skLineSegment(sketch, "E142.left", {"start": v(208.08, 7.15) * mm, "end": v(208.08, 18.15) * mm});
            skLineSegment(sketch, "E142.right", {"start": v(210.08, 7.15) * mm, "end": v(210.08, 18.15) * mm});
            skLineSegment(sketch, "E143.bottom", {"start": v(212.82, 7.15) * mm, "end": v(214.82, 7.15) * mm});
            skLineSegment(sketch, "E143.top", {"start": v(212.82, 18.15) * mm, "end": v(214.82, 18.15) * mm});
            skLineSegment(sketch, "E143.left", {"start": v(212.82, 7.15) * mm, "end": v(212.82, 18.15) * mm});
            skLineSegment(sketch, "E143.right", {"start": v(214.82, 7.15) * mm, "end": v(214.82, 18.15) * mm});
            skSolve(sketch);
        }
        {
            var Q0;
            Q0=qSketchRegion(id+"F43",true);
            extrude(context, id + "F44", {"entities" : qUnion([Q0]), "operationType" : NewBodyOperationType.ADD, "depth" : 2 * mm});
        }
        {
            var Q0;
            Q0=makeQuery(id+"F44.opExtrude","CAP_FACE",FACE,{"disambiguationData":[OSD([sQuery(id+"F43.wireOp",EDGE,"E141")])],"isStart":false});
            var sketch = newSketch(context, id + "F45", { "sketchPlane" : qUnion([Q0])});
            skCircle(sketch, "E144", {"center": v(192.46, 27.04) * mm, "radius": 3.3 * mm});
            skSolve(sketch);
        }
        {
            var Q0;
            Q0=qSketchRegion(id+"F45",true);
            extrude(context, id + "F46", {"entities" : qUnion([Q0]), "operationType" : NewBodyOperationType.REMOVE, "oppositeDirection" : true, "depth" : 19 * mm});
        }
        {
            var Q0;
            Q0=makeQuery(id+"F44.opExtrude","CAP_FACE",FACE,{"disambiguationData":[OSD([sQuery(id+"F43.wireOp",EDGE,"E139")])],"isStart":false});
            var sketch = newSketch(context, id + "F47", { "sketchPlane" : qUnion([Q0])});
            skCircle(sketch, "E145", {"center": v(192.46, 8.04) * mm, "radius": 3.3 * mm});
            skSolve(sketch);
        }
        {
            var Q0;
            Q0=qSketchRegion(id+"F47",true);
            extrude(context, id + "F48", {"entities" : qUnion([Q0]), "operationType" : NewBodyOperationType.REMOVE, "oppositeDirection" : true, "depth" : 20 * mm});
        }
        {
            var Q0;
            Q0=makeQuery(id+"F14.imprint","IMPRINT",FACE,{"disambiguationData":[TD([[makeQuery(id+"F14.imprint","IMPRINT",EDGE,{"derivedFrom":sQuery(id+"F14.wireOp",EDGE,"E16")}),1.0]])]});
            var sketch = newSketch(context, id + "F49", { "sketchPlane" : qUnion([Q0])});
            skLineSegment(sketch, "E146.bottom", {"start": v(29.08, 3.54) * mm, "end": v(58.08, 3.54) * mm});
            skLineSegment(sketch, "E146.top", {"start": v(29.08, 7.54) * mm, "end": v(58.08, 7.54) * mm});
            skLineSegment(sketch, "E146.left", {"start": v(29.08, 3.54) * mm, "end": v(29.08, 7.54) * mm});
            skLineSegment(sketch, "E146.right", {"start": v(58.08, 3.54) * mm, "end": v(58.08, 7.54) * mm});
            skLineSegment(sketch, "E147.bottom", {"start": v(58.08, 7.54) * mm, "end": v(144.08, 7.54) * mm});
            skLineSegment(sketch, "E147.top", {"start": v(58.08, 5.54) * mm, "end": v(144.08, 5.54) * mm});
            skLineSegment(sketch, "E147.left", {"start": v(58.08, 7.54) * mm, "end": v(58.08, 5.54) * mm});
            skLineSegment(sketch, "E147.right", {"start": v(144.08, 7.54) * mm, "end": v(144.08, 5.54) * mm});
            skSolve(sketch);
        }
        {
            var Q0;
            Q0=qSketchRegion(id+"F49",true);
            var Q1;
            Q1=sQuery(id+"F49.wireOp",EDGE,"E146.top");
            revolve(context, id + "F50", {"operationType" : NewBodyOperationType.REMOVE, "entities" : qUnion([Q0]), "axis" : qUnion([Q1]), "revolveType" : RevolveType.FULL, "oppositeDirection" : true});
        }
        {
            var Q0;
            Q0=makeQuery(id+"F44.opExtrude","CAP_FACE",FACE,{"disambiguationData":[OSD([sQuery(id+"F43.wireOp",EDGE,"E142.bottom"),sQuery(id+"F43.wireOp",EDGE,"E142.top"),sQuery(id+"F43.wireOp",EDGE,"E142.left"),sQuery(id+"F43.wireOp",EDGE,"E142.right")])],"isStart":false});
            var Q1;
            Q1=makeQuery(id+"F44.opExtrude","CAP_FACE",FACE,{"disambiguationData":[OSD([sQuery(id+"F43.wireOp",EDGE,"E143.bottom"),sQuery(id+"F43.wireOp",EDGE,"E143.top"),sQuery(id+"F43.wireOp",EDGE,"E143.left"),sQuery(id+"F43.wireOp",EDGE,"E143.right")])],"isStart":false});
            var Q2;
            Q2=makeQuery(id+"F44.opExtrude","CAP_EDGE",EDGE,{"disambiguationData":[OSD([sQuery(id+"F43.wireOp",EDGE,"E143.top")])],"isStart":false});
            revolve(context, id + "F51", {"operationType" : NewBodyOperationType.REMOVE, "entities" : qUnion([Q0, Q1]), "axis" : qUnion([Q2]), "revolveType" : RevolveType.FULL, "oppositeDirection" : true});
        }
        {
            var Q0;
            Q0=makeQuery(id+"F14.imprint","IMPRINT",FACE,{"disambiguationData":[TD([[makeQuery(id+"F14.imprint","IMPRINT",EDGE,{"derivedFrom":sQuery(id+"F14.wireOp",EDGE,"E16")}),1.0]])]});
            var sketch = newSketch(context, id + "F52", { "sketchPlane" : qUnion([Q0])});
            skLineSegment(sketch, "E148.bottom", {"start": v(197.96, 118.46) * mm, "end": v(205.96, 118.46) * mm});
            skLineSegment(sketch, "E148.top", {"start": v(197.96, 108.46) * mm, "end": v(205.96, 108.46) * mm});
            skLineSegment(sketch, "E148.left", {"start": v(197.96, 118.46) * mm, "end": v(197.96, 108.46) * mm});
            skLineSegment(sketch, "E148.right", {"start": v(205.96, 118.46) * mm, "end": v(205.96, 108.46) * mm});
            skLineSegment(sketch, "E149.bottom", {"start": v(197.96, 108.46) * mm, "end": v(209.96, 108.46) * mm});
            skLineSegment(sketch, "E149.top", {"start": v(197.96, 102.46) * mm, "end": v(209.96, 102.46) * mm});
            skLineSegment(sketch, "E149.left", {"start": v(197.96, 108.46) * mm, "end": v(197.96, 102.46) * mm});
            skLineSegment(sketch, "E149.right", {"start": v(209.96, 108.46) * mm, "end": v(209.96, 102.46) * mm});
            skLineSegment(sketch, "E150.bottom", {"start": v(197.96, 102.46) * mm, "end": v(203.46, 102.46) * mm});
            skLineSegment(sketch, "E150.top", {"start": v(197.96, 39.46) * mm, "end": v(203.46, 39.46) * mm});
            skLineSegment(sketch, "E150.left", {"start": v(197.96, 102.46) * mm, "end": v(197.96, 39.46) * mm});
            skLineSegment(sketch, "E150.right", {"start": v(203.46, 102.46) * mm, "end": v(203.46, 39.46) * mm});
            skSolve(sketch);
        }
        {
            var Q0;
            Q0=qSketchRegion(id+"F52",true);
            var Q1;
            Q1=sQuery(id+"F52.wireOp",EDGE,"E150.left");
            revolve(context, id + "F53", {"operationType" : NewBodyOperationType.REMOVE, "entities" : qUnion([Q0]), "axis" : qUnion([Q1]), "revolveType" : RevolveType.FULL, "oppositeDirection" : true});
        }
        {
            var Q0;
            Q0=makeQuery(id+"F53.boolean.opBoolean","COPY",EDGE,{"derivedFrom":makeQuery(id+"F53.opRevolve","SWEPT_EDGE",EDGE,{"disambiguationData":[OSD([sQuery(id+"F52.wireOp",EDGE,"E149.top"),sQuery(id+"F52.wireOp",EDGE,"E150.bottom"),sQuery(id+"F52.wireOp",EDGE,"E150.right")])]})});
            fillet(context, id + "F54", {"entities" : qUnion([Q0]), "radius" : 6 * mm, "tangentPropagation" : true, "allowEdgeOverflow" : false});
        }
        {
            var Q0;
            Q0=makeQuery(id+"F44.opExtrude","SWEPT_FACE",FACE,{"disambiguationData":[OSD([sQuery(id+"F43.wireOp",EDGE,"E143.bottom")])]});
            var sketch = newSketch(context, id + "F55", { "sketchPlane" : qUnion([Q0])});
            skLineSegment(sketch, "E151.bottom", {"start": v(214.82, 20) * mm, "end": v(207.95, 20) * mm});
            skLineSegment(sketch, "E151.top", {"start": v(214.82, 22.16) * mm, "end": v(207.95, 22.16) * mm});
            skLineSegment(sketch, "E151.left", {"start": v(214.82, 20) * mm, "end": v(214.82, 22.16) * mm});
            skLineSegment(sketch, "E151.right", {"start": v(207.95, 20) * mm, "end": v(207.95, 22.16) * mm});
            skSolve(sketch);
        }
        {
            var Q0;
            Q0 = qSketchRegion(id + "F55", true);
            extrude(context, id + "F56", {"entities" : qUnion([Q0]), "operationType" : NewBodyOperationType.REMOVE, "oppositeDirection" : true, "depth" : 2 * mm});
        }
    });
